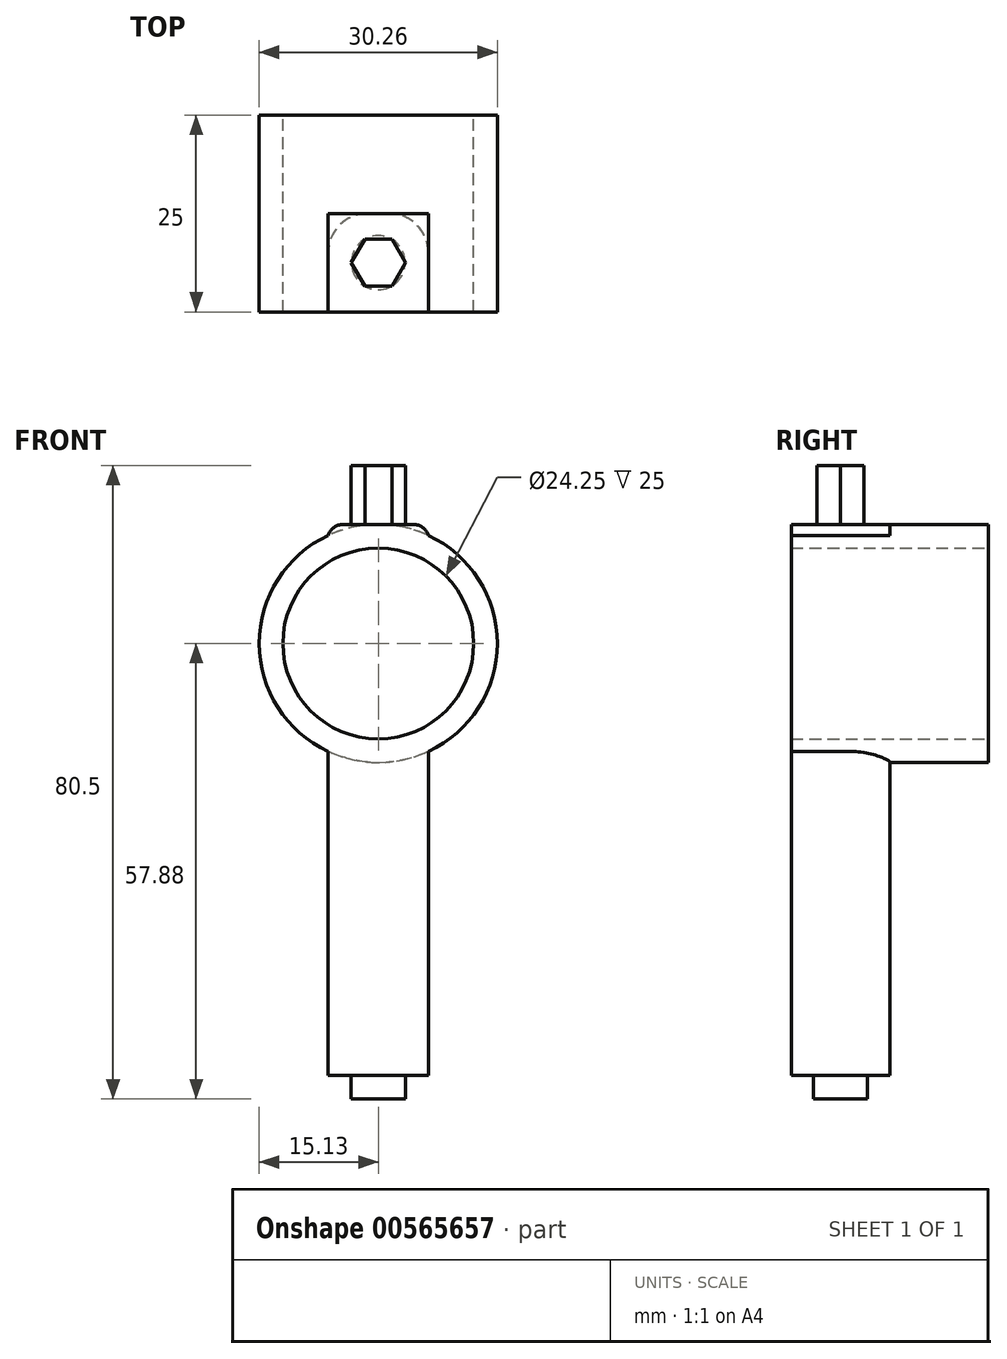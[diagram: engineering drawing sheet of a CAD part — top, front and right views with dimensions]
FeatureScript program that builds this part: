
annotation { "Feature Type Name" : "Feature", "Feature Type Description" : "" }
export const myFeature = defineFeature(function(context is Context, id is Id, definition is map)
    precondition{}
    {
        {
            var Q0;
            Q0=qCreatedBy(makeId("Front.planeOp"),FACE);
            var sketch = newSketch(context, id + "F0", { "sketchPlane" : qUnion([Q0])});
            skLineSegment(sketch, "E0.bottom", {"start": v(-6.37, 15.12) * mm, "end": v(6.37, 15.12) * mm});
            skLineSegment(sketch, "E0.top", {"start": v(-6.37, 12.12) * mm, "end": v(6.37, 12.12) * mm});
            skLineSegment(sketch, "E0.left", {"start": v(-6.37, 15.12) * mm, "end": v(-6.37, 12.12) * mm});
            skLineSegment(sketch, "E0.right", {"start": v(6.37, 15.12) * mm, "end": v(6.37, 12.12) * mm});
            skPoint(sketch, "E0.middle", {"position": v(0, 13.62) * mm});
            skLineSegment(sketch, "E1.bottom", {"start": v(-6.37, -54.88) * mm, "end": v(6.37, -54.88) * mm});
            skLineSegment(sketch, "E1.top", {"start": v(-6.37, -12.12) * mm, "end": v(6.37, -12.12) * mm});
            skLineSegment(sketch, "E1.left", {"start": v(-6.37, -54.88) * mm, "end": v(-6.37, -12.12) * mm});
            skLineSegment(sketch, "E1.right", {"start": v(6.37, -54.88) * mm, "end": v(6.37, -12.12) * mm});
            skPoint(sketch, "E1.middle", {"position": v(0, -33.5) * mm});
            skCircle(sketch, "E2", {"center": v(0, 0) * mm, "radius": 12.12 * mm});
            skLineSegment(sketch, "E3", {"start": v(0, 13.62) * mm, "end": v(0, -33.5) * mm, "construction": true});
            skCircle(sketch, "E4.0", {"center": v(0, 0) * mm, "radius": 15.12 * mm});
            skSolve(sketch);
        }
        {
            var Q0;
            {var subQ0=sQuery(id+"F0.wireOp",EDGE,"E1.left");var subQ1=sQuery(id+"F0.wireOp",EDGE,"E1.top");var subQ2=makeQuery(id+"F0.imprint","INTERSECT",VERTEX,{"derivedFrom":[subQ1,subQ0]});Q0=makeQuery(id+"F0.imprint","IMPRINT",FACE,{"disambiguationData":[TD([[makeQuery(id+"F0.imprint","IMPRINT",EDGE,{"disambiguationData":[TD([[subQ2,-1.0]])],"derivedFrom":subQ1}),-1.0]])]});}
            var Q1;
            {var subQ0=sQuery(id+"F0.wireOp",EDGE,"E0.left");var subQ1=sQuery(id+"F0.wireOp",EDGE,"E0.top");var subQ2=makeQuery(id+"F0.imprint","INTERSECT",VERTEX,{"derivedFrom":[subQ1,subQ0]});Q1=makeQuery(id+"F0.imprint","IMPRINT",FACE,{"disambiguationData":[TD([[makeQuery(id+"F0.imprint","IMPRINT",EDGE,{"disambiguationData":[TD([[subQ2,-1.0]])],"derivedFrom":subQ1}),1.0]])]});}
            var Q2;
            {var subQ5=sQuery(id+"F0.wireOp",EDGE,"E0.right");var subQ6=sQuery(id+"F0.wireOp",EDGE,"E0.top");var subQ7=makeQuery(id+"F0.imprint","INTERSECT",VERTEX,{"derivedFrom":[subQ6,subQ5]});Q2=makeQuery(id+"F0.imprint","IMPRINT",FACE,{"disambiguationData":[TD([[makeQuery(id+"F0.imprint","IMPRINT",EDGE,{"disambiguationData":[TD([[subQ7,1.0]])],"derivedFrom":subQ6}),-1.0]])]});}
            var Q3;
            {var subQ5=sQuery(id+"F0.wireOp",EDGE,"E0.left");var subQ6=sQuery(id+"F0.wireOp",EDGE,"E0.top");var subQ7=makeQuery(id+"F0.imprint","INTERSECT",VERTEX,{"derivedFrom":[subQ6,subQ5]});Q3=makeQuery(id+"F0.imprint","IMPRINT",FACE,{"disambiguationData":[TD([[makeQuery(id+"F0.imprint","IMPRINT",EDGE,{"disambiguationData":[TD([[subQ7,-1.0]])],"derivedFrom":subQ6}),-1.0]])]});}
            extrude(context, id + "F1", {"entities" : qUnion([Q0, Q1, Q2, Q3]), "endBound" : BoundingType.SYMMETRIC, "depth" : 25 * mm, "offsetDistance" : 25 * mm});
        }
        {
            var Q0;
            {var subQ0=sQuery(id+"F0.wireOp",EDGE,"E1.bottom");Q0=makeQuery(id+"F0.imprint","IMPRINT",FACE,{"disambiguationData":[TD([[makeQuery(id+"F0.imprint","IMPRINT",EDGE,{"derivedFrom":subQ0}),1.0]])]});}
            var Q1;
            Q1=makeQuery(id+"F1.opExtrude","CAP_FACE",FACE,{"disambiguationData":[OSD([sQuery(id+"F0.wireOp",EDGE,"E2"),sQuery(id+"F0.wireOp",EDGE,"E4.0")])],"isStart":false});
            extrude(context, id + "F2", {"entities" : qUnion([Q0]), "operationType" : NewBodyOperationType.ADD, "endBound" : BoundingType.UP_TO_SURFACE, "depth" : 10 * mm, "endBoundEntityFace" : qUnion([Q1]), "offsetDistance" : 25 * mm});
        }
        {
            var Q0;
            {var subQ0=sQuery(id+"F0.wireOp",EDGE,"E0.right");var subQ1=sQuery(id+"F0.wireOp",EDGE,"E0.bottom");var subQ2=makeQuery(id+"F0.imprint","INTERSECT",VERTEX,{"derivedFrom":[subQ1,subQ0]});Q0=makeQuery(id+"F0.imprint","IMPRINT",FACE,{"disambiguationData":[TD([[makeQuery(id+"F0.imprint","IMPRINT",EDGE,{"disambiguationData":[TD([[subQ2,1.0]])],"derivedFrom":subQ1}),-1.0]])]});}
            var Q1;
            {var subQ0=sQuery(id+"F0.wireOp",EDGE,"E0.left");var subQ1=sQuery(id+"F0.wireOp",EDGE,"E0.bottom");var subQ2=makeQuery(id+"F0.imprint","INTERSECT",VERTEX,{"derivedFrom":[subQ1,subQ0]});Q1=makeQuery(id+"F0.imprint","IMPRINT",FACE,{"disambiguationData":[TD([[makeQuery(id+"F0.imprint","IMPRINT",EDGE,{"disambiguationData":[TD([[subQ2,-1.0]])],"derivedFrom":subQ1}),-1.0]])]});}
            var Q2;
            {var subQ0=sQuery(id+"F0.wireOp",EDGE,"E4.0");var subQ1=sQuery(id+"F0.wireOp",EDGE,"E2");Q2=makeQuery(id+"F2.boolean.opBoolean","MERGE",FACE,{"derivedFrom":[makeQuery(id+"F1.opExtrude","CAP_FACE",FACE,{"disambiguationData":[OSD([subQ1,subQ0])],"isStart":false}),makeQuery(id+"F2.opExtrude","CAP_FACE",FACE,{"disambiguationData":[OSD([subQ1,subQ0])],"isStart":false})]});}
            extrude(context, id + "F3", {"entities" : qUnion([Q0, Q1]), "operationType" : NewBodyOperationType.ADD, "endBound" : BoundingType.UP_TO_SURFACE, "depth" : 25 * mm, "endBoundEntityFace" : qUnion([Q2]), "offsetDistance" : 25 * mm});
        }
        {
            var Q0;
            {var subQ0=sQuery(id+"F0.wireOp",EDGE,"E0.bottom");Q0=makeQuery(id+"F3.boolean.opBoolean","MERGE",FACE,{"derivedFrom":[makeQuery(id+"F3.opExtrude","SWEPT_FACE",FACE,{"disambiguationData":[OSD([subQ0]),TDD([makeQuery(id+"F0.imprint","IMPRINT",EDGE,{"disambiguationData":[TD([[makeQuery(id+"F0.imprint","INTERSECT",VERTEX,{"derivedFrom":[subQ0,sQuery(id+"F0.wireOp",EDGE,"E0.left")]}),-1.0]])],"derivedFrom":subQ0})])]}),makeQuery(id+"F3.opExtrude","SWEPT_FACE",FACE,{"disambiguationData":[OSD([subQ0]),TDD([makeQuery(id+"F0.imprint","IMPRINT",EDGE,{"disambiguationData":[TD([[makeQuery(id+"F0.imprint","INTERSECT",VERTEX,{"derivedFrom":[subQ0,sQuery(id+"F0.wireOp",EDGE,"E0.right")]}),1.0]])],"derivedFrom":subQ0})])]})]});}
            var sketch = newSketch(context, id + "F4", { "sketchPlane" : qUnion([Q0])});
            skCircle(sketch, "E5.cCircle", {"center": v(0, -6.25) * mm, "radius": 3.43 * mm, "construction": true});
            skLineSegment(sketch, "E5.0", {"start": v(3.43, -6.25) * mm, "end": v(1.71, -9.22) * mm});
            skLineSegment(sketch, "E5.1", {"start": v(1.71, -9.22) * mm, "end": v(-1.71, -9.22) * mm});
            skLineSegment(sketch, "E5.2", {"start": v(-1.71, -9.22) * mm, "end": v(-3.43, -6.25) * mm});
            skLineSegment(sketch, "E5.3", {"start": v(-3.43, -6.25) * mm, "end": v(-1.71, -3.28) * mm});
            skLineSegment(sketch, "E5.4", {"start": v(-1.71, -3.28) * mm, "end": v(1.71, -3.28) * mm});
            skLineSegment(sketch, "E5.5", {"start": v(1.71, -3.28) * mm, "end": v(3.43, -6.25) * mm});
            skLineSegment(sketch, "E6", {"start": v(0, 0) * mm, "end": v(0, -12.5) * mm, "construction": true});
            skLineSegment(sketch, "E7", {"start": v(-6.37, -6.25) * mm, "end": v(6.37, -6.25) * mm, "construction": true});
            skLineSegment(sketch, "E8", {"start": v(-6.37, 0) * mm, "end": v(6.37, 0) * mm, "construction": true});
            skLineSegment(sketch, "E9", {"start": v(-6.37, 0) * mm, "end": v(-6.37, -12.5) * mm, "construction": true});
            skLineSegment(sketch, "E10", {"start": v(-6.37, -12.5) * mm, "end": v(6.37, -12.5) * mm, "construction": true});
            skLineSegment(sketch, "E11", {"start": v(6.37, -12.5) * mm, "end": v(6.37, 0) * mm, "construction": true});
            skSolve(sketch);
        }
        {
            var Q0;
            Q0=makeQuery(id+"F2.opExtrude","SWEPT_FACE",FACE,{"disambiguationData":[OSD([sQuery(id+"F0.wireOp",EDGE,"E1.bottom")])]});
            var sketch = newSketch(context, id + "F5", { "sketchPlane" : qUnion([Q0])});
            skLineSegment(sketch, "E12", {"start": v(-6.37, 6.25) * mm, "end": v(6.37, 6.25) * mm, "construction": true});
            skCircle(sketch, "E13", {"center": v(0, 6.25) * mm, "radius": 3.43 * mm});
            skLineSegment(sketch, "E14", {"start": v(6.37, 12.5) * mm, "end": v(-6.37, 12.5) * mm, "construction": true});
            skLineSegment(sketch, "E15", {"start": v(-6.37, 12.5) * mm, "end": v(-6.37, 0) * mm, "construction": true});
            skLineSegment(sketch, "E16", {"start": v(-6.37, 0) * mm, "end": v(6.37, 0) * mm, "construction": true});
            skLineSegment(sketch, "E17", {"start": v(6.37, 0) * mm, "end": v(6.37, 12.5) * mm, "construction": true});
            skLineSegment(sketch, "E18", {"start": v(0, 12.5) * mm, "end": v(0, 0) * mm, "construction": true});
            skSolve(sketch);
        }
        {
            var Q0;
            Q0=makeQuery(id+"F4.imprint","IMPRINT",FACE,{"disambiguationData":[TD([[makeQuery(id+"F4.imprint","IMPRINT",EDGE,{"derivedFrom":sQuery(id+"F4.wireOp",EDGE,"E5.0")}),-1.0]])]});
            extrude(context, id + "F6", {"entities" : qUnion([Q0]), "operationType" : NewBodyOperationType.ADD, "depth" : (15 / 2) * mm, "offsetDistance" : 25 * mm});
        }
        {
            var Q0;
            Q0=makeQuery(id+"F5.imprint","IMPRINT",FACE,{"disambiguationData":[TD([[makeQuery(id+"F5.imprint","IMPRINT",EDGE,{"derivedFrom":sQuery(id+"F5.wireOp",EDGE,"E13")}),1.0]])]});
            extrude(context, id + "F7", {"entities" : qUnion([Q0]), "operationType" : NewBodyOperationType.ADD, "depth" : 3 * mm, "offsetDistance" : 25 * mm});
        }
        {
            var Q0;
            Q0=makeQuery(id+"F2.opExtrude","CAP_EDGE",EDGE,{"disambiguationData":[OSD([sQuery(id+"F0.wireOp",EDGE,"E0.right")])],"isStart":true});
            var Q1;
            Q1=makeQuery(id+"F2.opExtrude","CAP_EDGE",EDGE,{"disambiguationData":[OSD([sQuery(id+"F0.wireOp",EDGE,"E0.left")])],"isStart":true});
            var Q2;
            Q2=makeQuery(id+"F2.opExtrude","CAP_EDGE",EDGE,{"disambiguationData":[OSD([sQuery(id+"F0.wireOp",EDGE,"E1.right")])],"isStart":true});
            var Q3;
            Q3=makeQuery(id+"F2.opExtrude","CAP_EDGE",EDGE,{"disambiguationData":[OSD([sQuery(id+"F0.wireOp",EDGE,"E1.left")])],"isStart":true});
            var Q4;
            {var subQ0=sQuery(id+"F0.wireOp",EDGE,"E4.0");var subQ1=sQuery(id+"F0.wireOp",EDGE,"E0.left");Q4=makeQuery(id+"F2.opExtrude","TWEAK_EDGE",EDGE,{"derivedFrom":[makeQuery(id+"F0.imprint","IMPRINT",EDGE,{"disambiguationData":[TD([[makeQuery(id+"F0.imprint","INTERSECT",VERTEX,{"derivedFrom":[sQuery(id+"F0.wireOp",EDGE,"E0.bottom"),subQ1]}),-1.0]])],"derivedFrom":subQ1}),makeQuery(id+"F1.opExtrude","CAP_FACE",FACE,{"disambiguationData":[OSD([sQuery(id+"F0.wireOp",EDGE,"E2"),subQ0])],"isStart":false})]});}
            var Q5;
            {var subQ0=sQuery(id+"F0.wireOp",EDGE,"E4.0");var subQ1=sQuery(id+"F0.wireOp",EDGE,"E0.right");Q5=makeQuery(id+"F2.opExtrude","TWEAK_EDGE",EDGE,{"derivedFrom":[makeQuery(id+"F0.imprint","IMPRINT",EDGE,{"disambiguationData":[TD([[makeQuery(id+"F0.imprint","INTERSECT",VERTEX,{"derivedFrom":[sQuery(id+"F0.wireOp",EDGE,"E0.bottom"),subQ1]}),-1.0]])],"derivedFrom":subQ1}),makeQuery(id+"F1.opExtrude","CAP_FACE",FACE,{"disambiguationData":[OSD([sQuery(id+"F0.wireOp",EDGE,"E2"),subQ0])],"isStart":false})]});}
            var Q6;
            {var subQ0=sQuery(id+"F0.wireOp",EDGE,"E4.0");var subQ1=sQuery(id+"F0.wireOp",EDGE,"E1.right");Q6=makeQuery(id+"F2.opExtrude","TWEAK_EDGE",EDGE,{"derivedFrom":[makeQuery(id+"F0.imprint","IMPRINT",EDGE,{"disambiguationData":[TD([[makeQuery(id+"F0.imprint","INTERSECT",VERTEX,{"derivedFrom":[sQuery(id+"F0.wireOp",EDGE,"E1.bottom"),subQ1]}),-1.0]])],"derivedFrom":subQ1}),makeQuery(id+"F1.opExtrude","CAP_FACE",FACE,{"disambiguationData":[OSD([sQuery(id+"F0.wireOp",EDGE,"E2"),subQ0])],"isStart":false})]});}
            var Q7;
            {var subQ0=sQuery(id+"F0.wireOp",EDGE,"E4.0");var subQ1=sQuery(id+"F0.wireOp",EDGE,"E1.left");Q7=makeQuery(id+"F2.opExtrude","TWEAK_EDGE",EDGE,{"derivedFrom":[makeQuery(id+"F0.imprint","IMPRINT",EDGE,{"disambiguationData":[TD([[makeQuery(id+"F0.imprint","INTERSECT",VERTEX,{"derivedFrom":[sQuery(id+"F0.wireOp",EDGE,"E1.bottom"),subQ1]}),-1.0]])],"derivedFrom":subQ1}),makeQuery(id+"F1.opExtrude","CAP_FACE",FACE,{"disambiguationData":[OSD([sQuery(id+"F0.wireOp",EDGE,"E2"),subQ0])],"isStart":false})]});}
            fillet(context, id + "F8", {"entities" : qUnion([Q0, Q1, Q2, Q3, Q4, Q5, Q6, Q7]), "radius" : 5 * mm, "tangentPropagation" : true, "allowEdgeOverflow" : false});
        }
        {
            var Q0;
            Q0=makeQuery(id+"F3.opExtrude","SWEPT_EDGE",EDGE,{"disambiguationData":[OSD([sQuery(id+"F0.wireOp",EDGE,"E0.bottom"),sQuery(id+"F0.wireOp",EDGE,"E0.left")])]});
            var Q1;
            Q1=makeQuery(id+"F3.opExtrude","SWEPT_EDGE",EDGE,{"disambiguationData":[OSD([sQuery(id+"F0.wireOp",EDGE,"E0.bottom"),sQuery(id+"F0.wireOp",EDGE,"E0.right")])]});
            fillet(context, id + "F9", {"entities" : qUnion([Q0, Q1]), "radius" : 2 * mm, "tangentPropagation" : true, "allowEdgeOverflow" : false});
        }
    });
